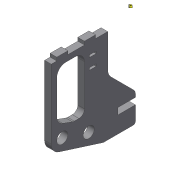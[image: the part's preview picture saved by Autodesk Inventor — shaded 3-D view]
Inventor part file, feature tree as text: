
AUTODESK INVENTOR PART (.ipt)
format: ipt  version: 2015 (Build 190159000, 159)  size: 189,440 bytes
history: native  units: mm
features: extrude x2, sketch x1
ambient origin geometry x8: Origin, YZ Plane, XZ Plane, XY Plane, X Axis, Y Axis, Z Axis, Center Point
bodies: Body1 (feature_tree)
feature tree (3):
  extrude  "Extrusion10"  Depth=10.0mm
  extrude  "Extrusion12"  Depth=3.0mm
  sketch  "Sketch1"  dims[d5=50.0mm d6=66.5mm d10=5.0mm d17=10.0mm d18=3.0mm d20=10.0mm d21=3.0mm d22=5.0mm d23=15.0mm d24=3.0mm d25=3.0mm d75=90.0deg d80=75.0mm d129=64.0mm d130=16.0mm d131=60.0mm d139=5.8mm d148=5.0mm d149=5.0mm d152=8.0mm d162=10.0mm d164=27.925268mm d167=55.0mm d169=5.0mm d170=5.0mm d171=8.0mm d173=10.0mm d174=6.0mm d175=0.0mm d184=5.0mm d185=30.0mm d186=135.0deg d187=10.0mm d188=5.0mm d189=25.0mm d190=15.0mm d191=25.0mm d192=2.0mm d202=10.0mm d203=0.0mm d204=2.0mm d205=6.0mm d206=8.0mm d207=4.5mm]
